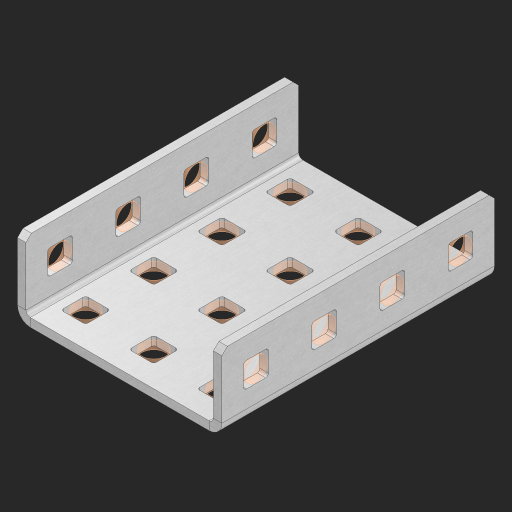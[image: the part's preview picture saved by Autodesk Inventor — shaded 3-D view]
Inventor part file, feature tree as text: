
AUTODESK INVENTOR PART (.ipt)
format: ipt  version: 2023 (Build 270158000, 158)  size: 628,736 bytes
history: native  units: in
note: dims shown in document units (in); Inventor stores cm internally (conversion verified against a paired STEP export)
features: other x25, extrude x19, sheet_metal_op x10, sketch x8, mirror x1, pattern_linear x1, chamfer x1
ambient origin geometry x8: Origin, YZ Plane, XZ Plane, XY Plane, X Axis, Y Axis, Z Axis, Center Point
bodies: Solid1 (feature_tree), Body (feature_tree)
feature tree (65):
  other  "Flange Pattern Plane"
  sheet_metal_op  "Flange Pattern"
  sheet_metal_op  "Body Pattern"
  other  "Arc Length"
  mirror  "Notch Mirror"
  pattern_linear  "Notch Pattern"  Spacing1=0.25in  [1 undecoded]
  chamfer  "End Chamfer"
  extrude  "Half Cut"  Depth=0.0625in
  sketch  "Sketch1"  dims[d0=1.5in]
  other  "Plate1"
  sketch  "Sketch2"  dims[d1=2.0in]
  other  "Plate2"
  sheet_metal_op  "Bend1"
  sheet_metal_op  "Corner1"
  sketch  "Sketch3"  dims[d2=0.0625in]
  other  "Flange Pattern Sketch"
  sketch  "Sketch7"  dims[d3=0.0625in]
  other  "Srf1"
  other  "Srf2"
  sketch  "Sketch8"  dims[d4=0.0312in]
  sketch  "Sketch9"  dims[d5=0.125in]
  other  "Srf91"
  sheet_metal_op  "Body Pattern Sketch"
  other  "Srf92"
  sketch  "Sketch13"  dims[d6=0.0625in]
  sketch  "Sketch14"  dims[d7=0.5in d8=90.0deg d9=0.0312in d10=0.25in d11=0.0625in d12=0.0625in d16=0.182in d17=0.02in d18=0.0625in d19=0.0in d20=0.25in d21=0.25in d46=0.172in d47=1.0in d48=0.0in d49=0.182in d50=0.02in d51=0.25in d52=0.25in d53=0.0625in d54=0.0in d55=0.172in d56=1.0in d57=0.0in d60=1.5748in d62=0.5in d63=1.1811in d65=0.5in d85=0.1473in d86=0.1782in d88=0.04in d89=0.0625in d90=0.0in d91=0.04in d92=0.0491in d95=2.5in d96=0.04in d97=0.25in d98=45.0deg d101=0.0in d102=2.497in d131=1.5in d132=1.5748in d134=0.5in d139=0.5in]
  other  "Srf856"
  other  "Srf1310"
  other  "Srf1311"
  other  "Srf1312"
  other  "Srf1376"
  other  "Srf1377"
  other  "Srf1728"
  other  "Srf1755"
  other  "Srf1878"
  other  "Srf1879"
  other  "Srf1942"
  other  "Srf1943"
  other  "Srf1944"
  other  "Srf1945"
  other  "Srf1946"
  other  "Srf1947"
  sheet_metal_op  "Flange Stamp"
  sheet_metal_op  "Flange Circle"
  sheet_metal_op  "Body Stamp"
  sheet_metal_op  "Body Circle"
  sheet_metal_op  "Notch"
  extrude  "ExtrusionSrf2"  Depth=0.0625in
  extrude  "ExtrusionSrf92"  Depth=0.182in
  extrude  "ExtrusionSrf856"  Depth=0.02in
  extrude  "ExtrusionSrf1310"  Depth=0.0625in
  extrude  "ExtrusionSrf1311"  TaperAngle=0.0deg  [1 undecoded]
  extrude  "ExtrusionSrf1312"  Depth=0.25in
  extrude  "ExtrusionSrf1376"  Depth=0.25in
  extrude  "ExtrusionSrf1377"  Depth=0.5in
  extrude  "ExtrusionSrf1728"  Depth=1.0in TaperAngle=0.0deg
  extrude  "ExtrusionSrf1755"  Depth=0.182in
  extrude  "ExtrusionSrf1878"  Depth=0.02in
  extrude  "ExtrusionSrf1879"  Depth=0.25in
  extrude  "ExtrusionSrf1942"  Depth=0.25in
  extrude  "ExtrusionSrf1943"  Depth=0.0625in
  extrude  "ExtrusionSrf1944"  TaperAngle=0.0deg  [1 undecoded]
  extrude  "ExtrusionSrf1945"  Depth=0.5in
  extrude  "ExtrusionSrf1946"  Depth=1.0in TaperAngle=0.0deg
  extrude  "ExtrusionSrf1947"  Depth=0.5in
note: 3 required parameter values undecoded (feature->parameter linkage not recoverable at this tier; creation-order binding heuristic only, values carry confidence <= 0.55)
